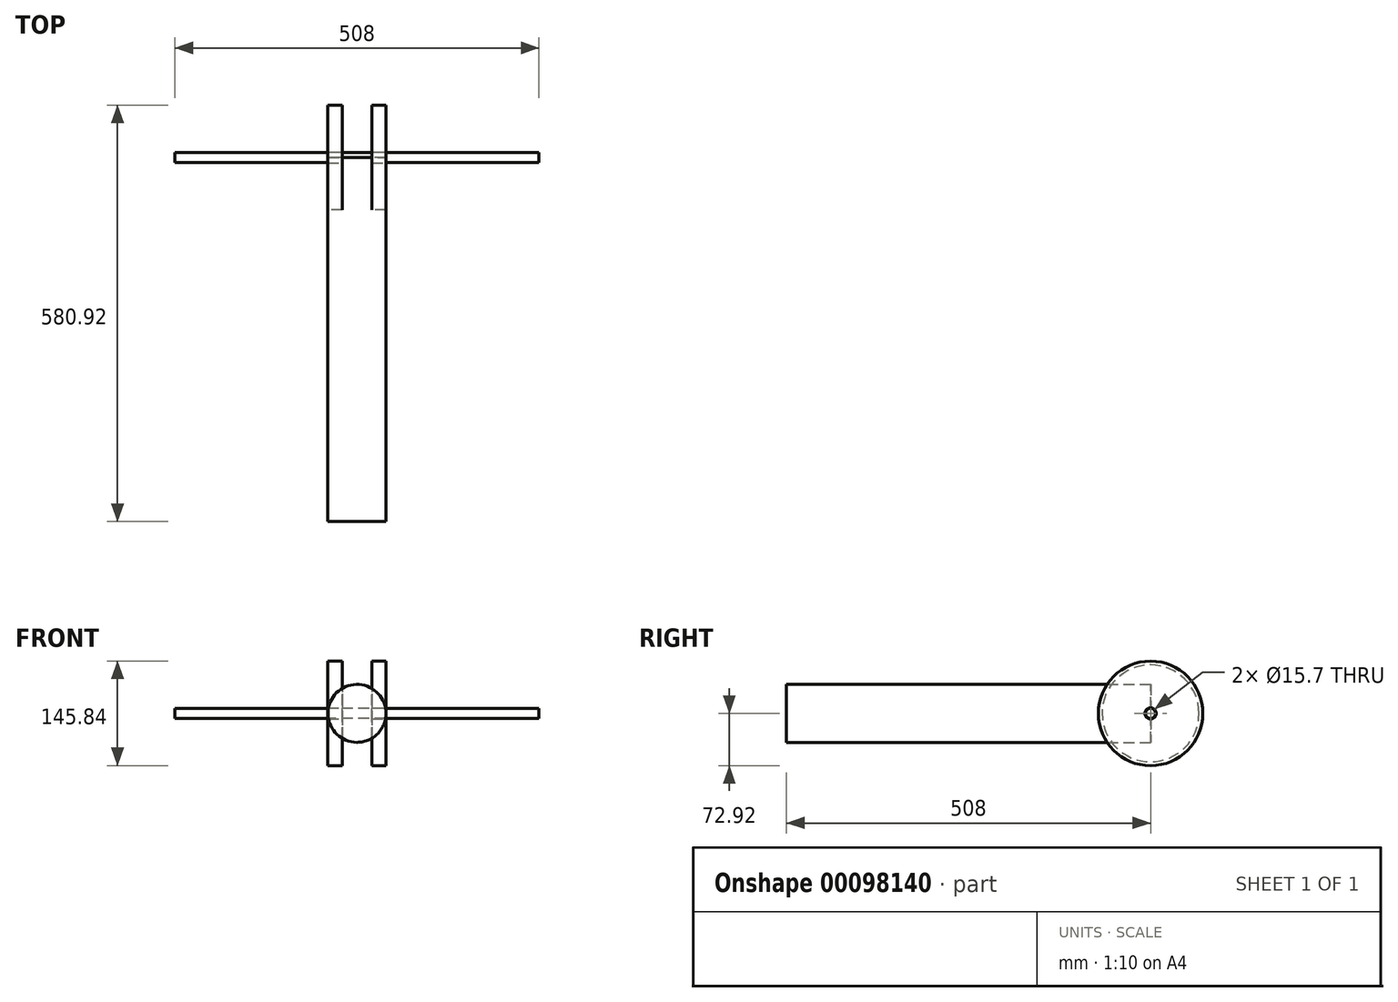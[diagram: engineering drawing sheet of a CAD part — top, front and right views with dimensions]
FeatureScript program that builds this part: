
annotation { "Feature Type Name" : "Feature", "Feature Type Description" : "" }
export const myFeature = defineFeature(function(context is Context, id is Id, definition is map)
    precondition{}
    {
        {
            var Q0;
            Q0=qCreatedBy(makeId("Front.planeOp"),FACE);
            var sketch = newSketch(context, id + "F0", { "sketchPlane" : qUnion([Q0])});
            skLineSegment(sketch, "E0", {"start": v(20.76, 67.6) * mm, "end": v(20.76, 6.58) * mm});
            skLineSegment(sketch, "E1", {"start": v(20.76, 6.58) * mm, "end": v(0, 6.58) * mm});
            skLineSegment(sketch, "E2", {"start": v(0, 6.58) * mm, "end": v(0, 0) * mm});
            skLineSegment(sketch, "E3", {"start": v(0, 0) * mm, "end": v(40.51, 0) * mm});
            skLineSegment(sketch, "E4", {"start": v(40.51, 0) * mm, "end": v(40.51, 72.92) * mm});
            skLineSegment(sketch, "E5", {"start": v(40.51, 72.92) * mm, "end": v(20.5, 72.92) * mm});
            skLineSegment(sketch, "E6", {"start": v(20.5, 72.92) * mm, "end": v(20.76, 67.6) * mm});
            skLineSegment(sketch, "E7.MirrorCS", {"start": v(-40.51, 0) * mm, "end": v(-40.51, 72.92) * mm});
            skLineSegment(sketch, "E8.MirrorCS", {"start": v(-40.51, 72.92) * mm, "end": v(-20.5, 72.92) * mm});
            skLineSegment(sketch, "E9.MirrorCS", {"start": v(-20.76, 67.6) * mm, "end": v(-20.76, 6.58) * mm});
            skLineSegment(sketch, "E10.MirrorCS", {"start": v(-20.5, 72.92) * mm, "end": v(-20.76, 67.6) * mm});
            skLineSegment(sketch, "E11.MirrorCS", {"start": v(-20.76, 6.58) * mm, "end": v(0, 6.58) * mm});
            skLineSegment(sketch, "E12.MirrorCS", {"start": v(0, 0) * mm, "end": v(-40.51, 0) * mm});
            skSolve(sketch);
        }
        {
            var Q0;
            Q0 = qSketchRegion(id + "F0", true);
            var Q1;
            Q1=sQuery(id+"F0.wireOp",EDGE,"E3");
            revolve(context, id + "F1", {"entities" : qUnion([Q0]), "axis" : qUnion([Q1]), "revolveType" : RevolveType.FULL});
        }
        {
            var Q0;
            Q0=makeQuery(id+"F1.opRevolve","SWEPT_FACE",FACE,{"disambiguationData":[OSD([sQuery(id+"F0.wireOp",EDGE,"E4")])]});
            var sketch = newSketch(context, id + "F2", { "sketchPlane" : qUnion([Q0])});
            skCircle(sketch, "E13", {"center": v(0, 0) * mm, "radius": 7.85 * mm});
            skSolve(sketch);
        }
        {
            var Q0;
            Q0 = qSketchRegion(id + "F2", true);
            extrude(context, id + "F3", {"entities" : qUnion([Q0]), "operationType" : NewBodyOperationType.REMOVE, "endBound" : BoundingType.THROUGH_ALL, "oppositeDirection" : true, "depth" : 25.4 * mm});
        }
        {
            var Q0;
            Q0=qCreatedBy(makeId("Front.planeOp"),FACE);
            var sketch = newSketch(context, id + "F4", { "sketchPlane" : qUnion([Q0])});
            skCircle(sketch, "E14", {"center": v(0, 0) * mm, "radius": 40.46 * mm});
            skSolve(sketch);
        }
        {
            var Q0;
            Q0 = qSketchRegion(id + "F4", true);
            extrude(context, id + "F5", {"entities" : qUnion([Q0]), "depth" : 508 * mm});
        }
        {
            var Q0;
            Q0=qCreatedBy(makeId("Right.planeOp"),FACE);
            var sketch = newSketch(context, id + "F6", { "sketchPlane" : qUnion([Q0])});
            skCircle(sketch, "E15", {"center": v(0, 0) * mm, "radius": 6.9 * mm});
            skSolve(sketch);
        }
        {
            var Q0;
            Q0 = qSketchRegion(id + "F6", true);
            extrude(context, id + "F7", {"entities" : qUnion([Q0]), "operationType" : NewBodyOperationType.ADD, "endBound" : BoundingType.SYMMETRIC, "depth" : 508 * mm});
        }
    });
